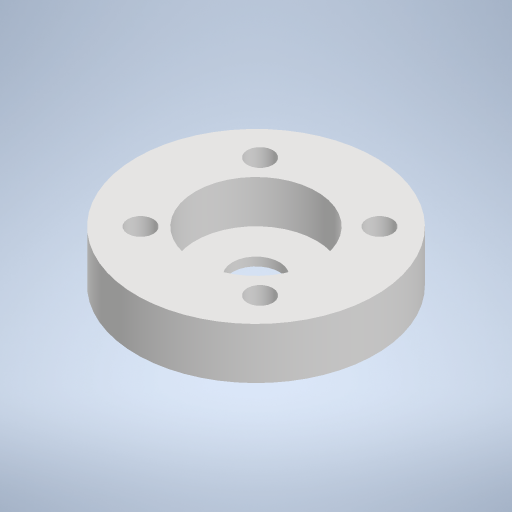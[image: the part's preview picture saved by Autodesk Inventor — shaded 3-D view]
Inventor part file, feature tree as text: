
AUTODESK INVENTOR PART (.ipt)
format: ipt  version: 2024.2 (Build 282272000, 272)  size: 266,240 bytes
history: native  units: mm
features: reference x4, extrude x3, other x3, sketch x2
ambient origin geometry x8: Origin, YZ Plane, XZ Plane, XY Plane, X Axis, Y Axis, Z Axis, Center Point
bodies: Body1 (feature_tree)
feature tree (12):
  sketch  "Эскиз1"
  extrude  "Выдавливание2"  Depth=28.0mm
  extrude  "Выдавливание3"  Depth=14.2mm
  extrude  "Выдавливание4"  Depth=5.5mm
  reference  "Ссылка1"
  reference  "Ссылка2"
  reference  "Ссылка3"
  reference  "Ссылка4"
  sketch  "Эскиз2"
  other  "<userpath>\Documents\Artist-v2\3D\Робот.iam"
  other  "Робот.iam"
  other  "бок:1"
